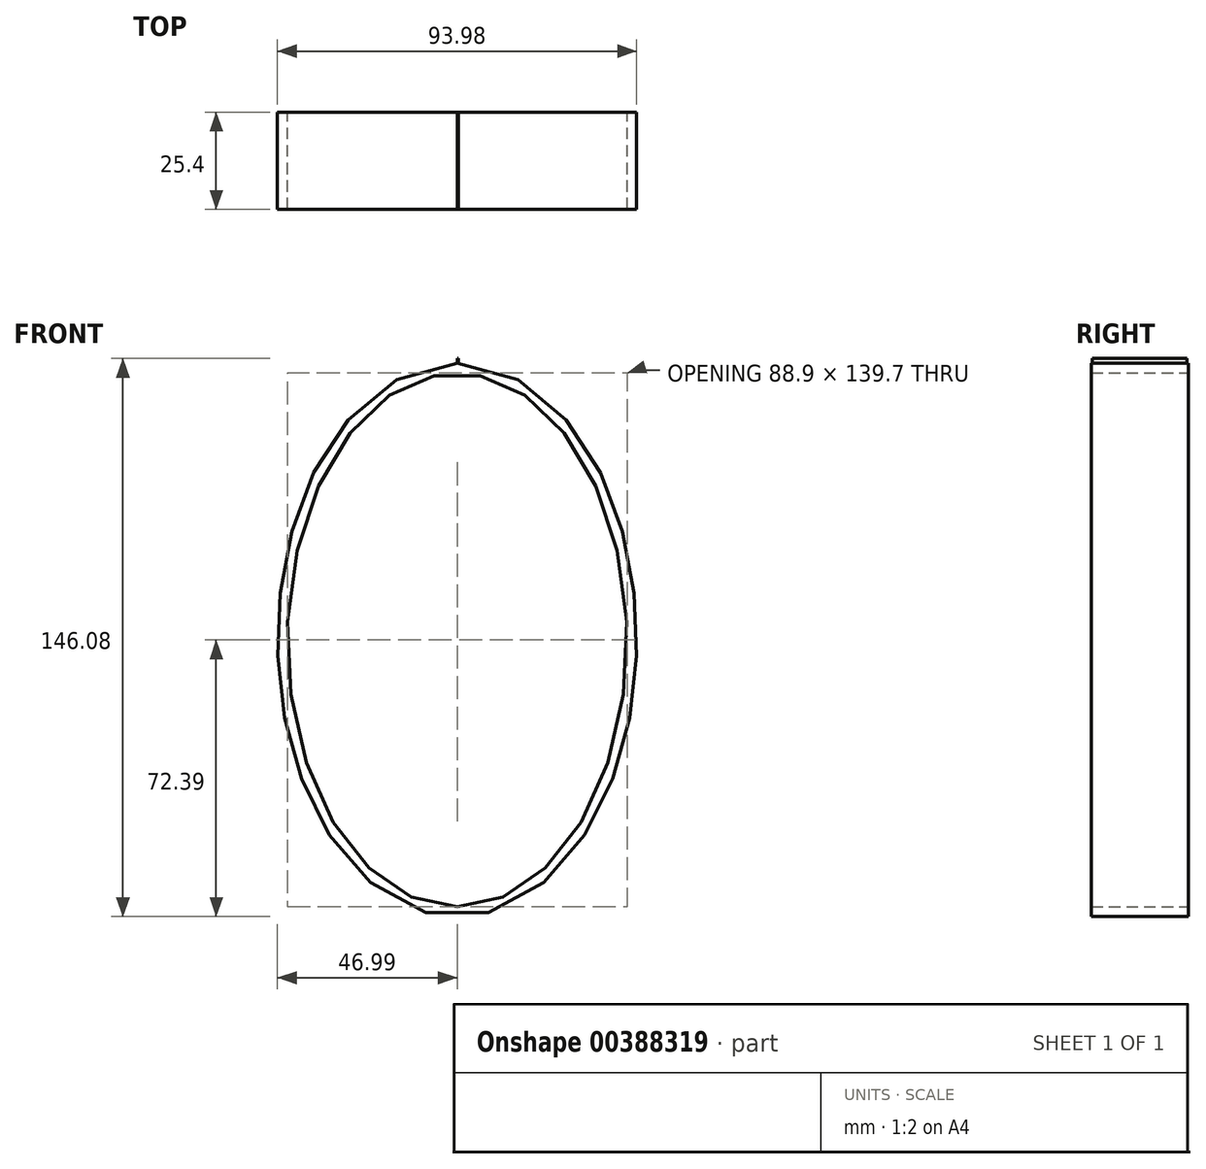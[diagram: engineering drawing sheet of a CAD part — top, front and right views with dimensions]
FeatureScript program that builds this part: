
annotation { "Feature Type Name" : "Feature", "Feature Type Description" : "" }
export const myFeature = defineFeature(function(context is Context, id is Id, definition is map)
    precondition{}
    {
        {
            var Q0;
            Q0=qCreatedBy(makeId("Front.planeOp"),FACE);
            var sketch = newSketch(context, id + "F0", { "sketchPlane" : qUnion([Q0])});
            skEllipse(sketch, "E0", {"center": v(0, 0) * mm, "majorRadius": 69.85 * mm, "minorRadius": 44.45 * mm, "majorAxis": v(0, -1)});
            skSolve(sketch);
        }
        {
            var Q0;
            Q0 = qSketchRegion(id + "F0", true);
            extrude(context, id + "F1", {"entities" : qUnion([Q0]), "depth" : 25.4 * mm});
        }
        {
            var Q0;
            Q0=makeQuery(id+"F1.opExtrude","CAP_FACE",FACE,{"disambiguationData":[OSD([sQuery(id+"F0.wireOp",EDGE,"E0")])],"isStart":false});
            var Q1;
            Q1=makeQuery(id+"F1.opExtrude","CAP_FACE",FACE,{"disambiguationData":[OSD([sQuery(id+"F0.wireOp",EDGE,"E0")])],"isStart":true});
            var Q2;
            Q2=makeQuery(id+"F1.opExtrude","SWEPT_BODY",BODY,{"disambiguationData":[OSD([sQuery(id+"F0.wireOp",EDGE,"E0")])]});
            shell(context, id + "F2", {"entities" : qUnion([Q0, Q1]), "parts" : qUnion([Q2]), "thickness" : 2.54 * mm, "oppositeDirection" : true});
        }
        {
            var Q0;
            Q0=qCreatedBy(makeId("Right.planeOp"),FACE);
            var sketch = newSketch(context, id + "F3", { "sketchPlane" : qUnion([Q0])});
            skLineSegment(sketch, "E1", {"start": v(-0.38, 72.14) * mm, "end": v(-25.13, 72.14) * mm});
            skLineSegment(sketch, "E2", {"start": v(-25.13, 72.14) * mm, "end": v(-25.13, 73.69) * mm});
            skLineSegment(sketch, "E3", {"start": v(-25.13, 73.69) * mm, "end": v(-0.38, 73.69) * mm});
            skLineSegment(sketch, "E4", {"start": v(-0.38, 73.69) * mm, "end": v(-0.38, 72.14) * mm});
            skSolve(sketch);
        }
        {
            var Q0;
            Q0=makeQuery(id+"F3.imprint","IMPRINT",FACE,{"disambiguationData":[TD([[makeQuery(id+"F3.imprint","IMPRINT",EDGE,{"derivedFrom":sQuery(id+"F3.wireOp",EDGE,"E1")}),-1.0]])]});
            extrude(context, id + "F4", {"entities" : qUnion([Q0]), "operationType" : NewBodyOperationType.ADD, "depth" : 0.25 * mm});
        }
    });
